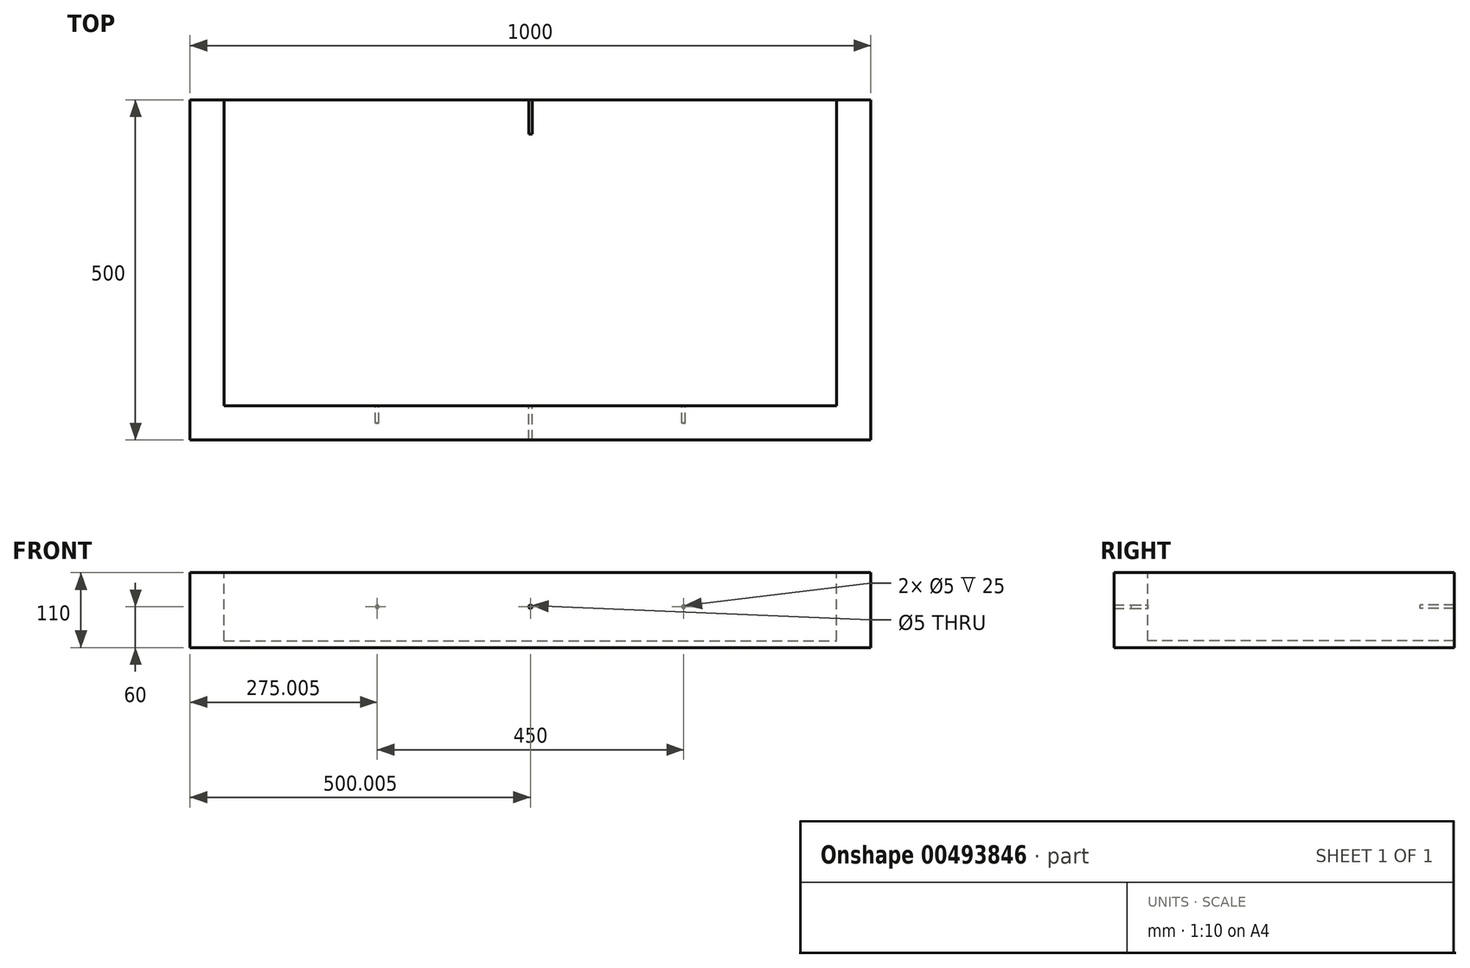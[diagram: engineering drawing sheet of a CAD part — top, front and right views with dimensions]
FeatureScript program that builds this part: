
annotation { "Feature Type Name" : "Feature", "Feature Type Description" : "" }
export const myFeature = defineFeature(function(context is Context, id is Id, definition is map)
    precondition{}
    {
        {
            var Q0;
            Q0=qCreatedBy(makeId("Top.planeOp"),FACE);
            var sketch = newSketch(context, id + "F0", { "sketchPlane" : qUnion([Q0])});
            skLineSegment(sketch, "E0.bottom", {"start": v(-142.93, 430.1) * mm, "end": v(857.07, 430.1) * mm});
            skLineSegment(sketch, "E0.top", {"start": v(-142.93, -69.9) * mm, "end": v(857.07, -69.9) * mm});
            skLineSegment(sketch, "E0.left", {"start": v(-142.93, 430.1) * mm, "end": v(-142.93, -69.9) * mm});
            skLineSegment(sketch, "E0.right", {"start": v(857.07, 430.1) * mm, "end": v(857.07, -69.9) * mm});
            skSolve(sketch);
        }
        {
            var Q0;
            Q0=makeQuery(id+"F0.imprint","IMPRINT",FACE,{"disambiguationData":[TD([[makeQuery(id+"F0.imprint","IMPRINT",EDGE,{"derivedFrom":sQuery(id+"F0.wireOp",EDGE,"E0.bottom")}),-1.0]])]});
            extrude(context, id + "F1", {"entities" : qUnion([Q0]), "depth" : 110 * mm});
        }
        {
            var Q0;
            Q0=makeQuery(id+"F1.opExtrude","CAP_FACE",FACE,{"disambiguationData":[OSD([sQuery(id+"F0.wireOp",EDGE,"E0.bottom"),sQuery(id+"F0.wireOp",EDGE,"E0.top"),sQuery(id+"F0.wireOp",EDGE,"E0.left"),sQuery(id+"F0.wireOp",EDGE,"E0.right")])],"isStart":false});
            var sketch = newSketch(context, id + "F2", { "sketchPlane" : qUnion([Q0])});
            skLineSegment(sketch, "E1", {"start": v(357.07, 430.1) * mm, "end": v(357.07, -69.9) * mm, "construction": true});
            skLineSegment(sketch, "E2.bottom", {"start": v(-92.93, 380.1) * mm, "end": v(807.07, 380.1) * mm});
            skLineSegment(sketch, "E2.top", {"start": v(-92.93, -19.9) * mm, "end": v(807.07, -19.9) * mm});
            skLineSegment(sketch, "E2.left", {"start": v(-92.93, 380.1) * mm, "end": v(-92.93, -19.9) * mm});
            skLineSegment(sketch, "E2.right", {"start": v(807.07, 380.1) * mm, "end": v(807.07, -19.9) * mm});
            skPoint(sketch, "E2.middle", {"position": v(357.07, 180.1) * mm});
            skSolve(sketch);
        }
        {
            var Q0;
            Q0=makeQuery(id+"F2.imprint","IMPRINT",FACE,{"disambiguationData":[TD([[makeQuery(id+"F2.imprint","IMPRINT",EDGE,{"derivedFrom":sQuery(id+"F2.wireOp",EDGE,"E2.bottom")}),-1.0]])]});
            extrude(context, id + "F3", {"entities" : qUnion([Q0]), "operationType" : NewBodyOperationType.REMOVE, "oppositeDirection" : true, "depth" : 100 * mm});
        }
        {
            var Q0;
            Q0=makeQuery(id+"F3.boolean.opBoolean","COPY",FACE,{"derivedFrom":makeQuery(id+"F3.opExtrude","SWEPT_FACE",FACE,{"disambiguationData":[OSD([sQuery(id+"F2.wireOp",EDGE,"E2.bottom")])]})});
            var sketch = newSketch(context, id + "F4", { "sketchPlane" : qUnion([Q0])});
            skLineSegment(sketch, "E3", {"start": v(357.07, 110) * mm, "end": v(357.07, 10) * mm});
            skCircle(sketch, "E4", {"center": v(357.07, 60) * mm, "radius": 2.5 * mm});
            skSolve(sketch);
        }
        {
            var Q0;
            {var subQ0=sQuery(id+"F4.wireOp",EDGE,"E4");var subQ1=sQuery(id+"F4.wireOp",EDGE,"E3");var subQ2=makeQuery(id+"F4.imprint","INTERSECT",VERTEX,{"disambiguationData":[OD(0.0)],"derivedFrom":[subQ1,subQ0]});Q0=makeQuery(id+"F4.imprint","IMPRINT",FACE,{"disambiguationData":[TD([[makeQuery(id+"F4.imprint","IMPRINT",EDGE,{"disambiguationData":[TD([[subQ2,-1.0]])],"derivedFrom":subQ1}),1.0]])]});}
            var Q1;
            {var subQ0=sQuery(id+"F4.wireOp",EDGE,"E4");var subQ1=sQuery(id+"F4.wireOp",EDGE,"E3");var subQ2=makeQuery(id+"F4.imprint","INTERSECT",VERTEX,{"disambiguationData":[OD(0.0)],"derivedFrom":[subQ1,subQ0]});Q1=makeQuery(id+"F4.imprint","IMPRINT",FACE,{"disambiguationData":[TD([[makeQuery(id+"F4.imprint","IMPRINT",EDGE,{"disambiguationData":[TD([[subQ2,-1.0]])],"derivedFrom":subQ1}),-1.0]])]});}
            var Q2;
            Q2=sQuery(id+"F4.wireOp",EDGE,"E4");
            extrude(context, id + "F5", {"entities" : qUnion([Q0, Q1]), "operationType" : NewBodyOperationType.REMOVE, "surfaceEntities" : qUnion([Q2]), "oppositeDirection" : true, "depth" : 50 * mm});
        }
        {
            var Q0;
            Q0=makeQuery(id+"F3.boolean.opBoolean","COPY",FACE,{"derivedFrom":makeQuery(id+"F3.opExtrude","SWEPT_FACE",FACE,{"disambiguationData":[OSD([sQuery(id+"F2.wireOp",EDGE,"E2.top")])]})});
            var sketch = newSketch(context, id + "F6", { "sketchPlane" : qUnion([Q0])});
            skLineSegment(sketch, "E5", {"start": v(-357.07, 110) * mm, "end": v(-357.07, 10) * mm, "construction": true});
            skCircle(sketch, "E6", {"center": v(-357.07, 60) * mm, "radius": 2.5 * mm});
            skSolve(sketch);
        }
        {
            var Q0;
            Q0=makeQuery(id+"F6.imprint","IMPRINT",FACE,{"disambiguationData":[TD([[makeQuery(id+"F6.imprint","IMPRINT",EDGE,{"derivedFrom":sQuery(id+"F6.wireOp",EDGE,"E6")}),1.0]])]});
            extrude(context, id + "F7", {"entities" : qUnion([Q0]), "operationType" : NewBodyOperationType.REMOVE, "oppositeDirection" : true, "depth" : 50 * mm});
        }
        {
            var Q0;
            Q0=makeQuery(id+"F3.boolean.opBoolean","COPY",FACE,{"derivedFrom":makeQuery(id+"F3.opExtrude","SWEPT_FACE",FACE,{"disambiguationData":[OSD([sQuery(id+"F2.wireOp",EDGE,"E2.bottom")])]})});
            var sketch = newSketch(context, id + "F8", { "sketchPlane" : qUnion([Q0])});
            skLineSegment(sketch, "E7", {"start": v(357.07, 60) * mm, "end": v(-92.93, 60) * mm, "construction": true});
            skLineSegment(sketch, "E8", {"start": v(357.07, 60) * mm, "end": v(807.07, 60) * mm, "construction": true});
            skCircle(sketch, "E9", {"center": v(132.07, 60) * mm, "radius": 2.5 * mm});
            skCircle(sketch, "E10", {"center": v(582.07, 60) * mm, "radius": 2.5 * mm});
            skSolve(sketch);
        }
        {
            var Q0;
            Q0=makeQuery(id+"F8.imprint","IMPRINT",FACE,{"disambiguationData":[TD([[makeQuery(id+"F8.imprint","IMPRINT",EDGE,{"derivedFrom":sQuery(id+"F8.wireOp",EDGE,"E9")}),1.0]])]});
            extrude(context, id + "F9", {"entities" : qUnion([Q0]), "operationType" : NewBodyOperationType.REMOVE, "oppositeDirection" : true, "depth" : 25 * mm});
        }
        {
            var Q0;
            Q0 = qSketchRegion(id + "F8", true);
            extrude(context, id + "F10", {"entities" : qUnion([Q0]), "operationType" : NewBodyOperationType.REMOVE, "oppositeDirection" : true, "depth" : 25 * mm});
        }
        {
            var Q0;
            Q0=makeQuery(id+"F3.boolean.opBoolean","COPY",FACE,{"derivedFrom":makeQuery(id+"F3.opExtrude","SWEPT_FACE",FACE,{"disambiguationData":[OSD([sQuery(id+"F2.wireOp",EDGE,"E2.top")])]})});
            var sketch = newSketch(context, id + "F11", { "sketchPlane" : qUnion([Q0])});
            skLineSegment(sketch, "E11", {"start": v(-357.07, 60) * mm, "end": v(-807.07, 60) * mm, "construction": true});
            skCircle(sketch, "E12", {"center": v(-582.07, 60) * mm, "radius": 2.5 * mm});
            skLineSegment(sketch, "E13", {"start": v(-357.07, 60) * mm, "end": v(92.93, 60) * mm, "construction": true});
            skCircle(sketch, "E14", {"center": v(-132.07, 60) * mm, "radius": 2.5 * mm});
            skSolve(sketch);
        }
        {
            var Q0;
            Q0=makeQuery(id+"F11.imprint","IMPRINT",FACE,{"disambiguationData":[TD([[makeQuery(id+"F11.imprint","IMPRINT",EDGE,{"derivedFrom":sQuery(id+"F11.wireOp",EDGE,"E14")}),1.0]])]});
            var Q1;
            Q1=makeQuery(id+"F11.imprint","IMPRINT",FACE,{"disambiguationData":[TD([[makeQuery(id+"F11.imprint","IMPRINT",EDGE,{"derivedFrom":sQuery(id+"F11.wireOp",EDGE,"E12")}),1.0]])]});
            extrude(context, id + "F12", {"entities" : qUnion([Q0, Q1]), "operationType" : NewBodyOperationType.REMOVE, "oppositeDirection" : true, "depth" : 25 * mm});
        }
    });
